# Revit family: WCPan-RimEx-WallHung-54cm-Vitra-İntegraSeries-7041
name_source: partatom
category: Plumbing Fixtures
revit_build: Autodesk Revit 2017 (Build: 20160225_1515(x64)
units: mm (PartAtom-declared; Revit-internal decimal feet)

## family parameters
Cut with Voids When Loaded = No
Host = Face
OmniClass Number = 23.45.05.21.11
OmniClass Title = Water Closets
Part Type = Normal
Room Calculation Point = No
Round Connector Dimension = Use Diameter
Shared = Yes

## types (9) — shared parameters
BIMobject category = Sanitary - Toilets
Brand = VitrA
CW Connection = Yes
Default Elevation = 410 mm
Design country = Turkey
HW Connection = No
IFC Classification = Sanitary Terminal
Main Material = Ceramic
Manufacturer = Vitra
Manufacturer name = Vitra
Masterformat 2014 Code = 22 45 26
Masterformat 2014 Description = Sanitary Facilities
Mounting type = Wall Hung
NBS Referans Code = 35-65-90
NBS Referans Description = Toilet Systems
Nominal Depth (mm) = 545 mm  [stored 1.78806 ft]
Nominal Height (mm) = 350 mm  [stored 1.14829 ft]
Nominal Width (mm) = 355 mm
OmniClass Code = 23-31 19 00
OmniClass Description = Toilets
Product certification = https://www.vitraglobal.com
Product family = İntegra
Product group = Wall Mounted WC
UNSPSC Description = Sanitary Ware
URL = https://www.vitra.com.tr
Uniclass 1.4 Code = L7216
Uniclass 1.4 Description = Toilets
Uniclass 2.0 Code = SS-35-65-90
Uniclass 2.0 Description = Toilet Systems
Uniclass 2015 Code = Pr_40_20_93
Uniclass 2015 Name = Urinal and WC fittings
Uniformat II Code = D2010
Uniformat II Description = Sanitary Facilities
Vent Connection = No
Warranty Period (Year) = 10 Years
Waste Connection = Yes
Weight Net (kg) = 28.3
Youtube = https://www.youtube.com

## per-type parameters (varying)
| type | Article No. (default) | Color | Description | Model | Primary Material | Product SKU | Product data url | Product url | Technical description |
| WCPan-WallHung-54cm-Vitra-İntegraSeries_7041B003-0075 | 7041B003-0075 | White | VitrA Integra Rim-Ex Wall-Hung WC - Without Bidet 54cm White | 7041B003-0075 | White | 7041B003-0075 | https://www.bimobject.com | https://www.vitraglobal.com | https://www.vitraglobal.com |
| WCPan-WallHung-54cm-Vitra-İntegraSeries_7041B003-0090 | 7041B003-0090 | White | VitrA Integra Rim-Ex Wall-Hung WC - Bidet entrance flush-mounted 54cm White | 7041B003-0090 | White | 7041B003-0090 |  | https://www.vitra.com.tr | https://www.vitra.com.tr |
| WCPan-WallHung-54cm-Vitra-İntegraSeries-7041B003-6200 | 7041B003-6200 | White | VitrA Integra Aquacare Rim-Ex Wall Hung WC - With Bidet Function 54cm White | 7041B003-6200 | White | 7041B003-6200 |  | https://www.vitraglobal.com | https://www.vitraglobal.com |
| WCPan-WallHung-54cm-Vitra-İntegraSeries-7041B003H0090 | 7041B003H0090 | White | VitrA Integra Rim-Ex Wall Hung WC - With Bidet Function 54cm White | 7041B003H0090 | White | 7041B003H0090 |  | https://www.vitra-india.com | https://www.vitra-india.com |
| WCPan-WallHung-54cm-Vitra-İntegraSeries-7041B420H0090 | 7041B420H0090 | Taupe | VitrA Integra Rim-Ex Wall Hung WC - With Bidet Function 54cm Taupe
With Bidet Function 54cm Taupe | 7041B420H0090 | Matte Taupe | 7041B420H0090 |  | https://www.vitra-india.com | https://www.vitra-india.com |
| WCPan-WallHung-54cm-Vitra-İntegraSeries-7041B483H0090 | 7041B483H0090 | Matte Black | VitrA Integra Rim-Ex Wall Hung WC - With Bidet Function 54m Matte Black
With Bidet Function 54cm Taupe | 7041B483H0090 | Matte Black | 7041B483H0090 |  | https://www.vitra-india.com | https://www.vitra-india.com |
| WCPan-WallHung-54cm-Vitra-İntegraSeries-7041B003H0075 | 7041B003H0075 | White | VitrA Integra Rim-Ex Wall Hung WC - Without Bidet Function 54cm White | 7041B003H0075 | White | 7041B003H0075 |  | https://www.vitra-india.com | https://www.vitra-india.com |
| WCPan-WallHung-54cm-Vitra-İntegraSeries-7041B420H0075 | 7041B420H0075 | Taupe | VitrA Integra Rim-Ex Wall Hung WC - Without Bidet Function 54cm White
With Bidet Function 54cm Taupe | 7041B420H0075 | Matte Taupe | 7041B420H0075 |  | https://www.vitra-india.com | https://www.vitra-india.com |
| WCPan-WallHung-54cm-Vitra-İntegraSeries-7041B483H0075 | 7041B483H0075 | Matte Black | VitrAIntegra Rim-Ex Wall Hung WC - Without Bidet Function, 54cm Matte Black
With Bidet Function 54cm Taupe | 7041B483H0075 | Matte Black | 7041B483H0075 |  | https://www.vitra-india.com | https://www.vitra-india.com |

note: [stored X ft] marks values corroborated as IEEE doubles in the binary element streams (Revit-internal decimal feet)

## geometry (parser evidence)
native form markers: Sweep x2
no freeform markers — native parametric forms only
